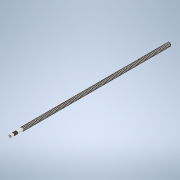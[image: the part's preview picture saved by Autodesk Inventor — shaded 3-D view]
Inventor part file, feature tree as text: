
AUTODESK INVENTOR PART (.ipt)
format: ipt  version: 2020.1 (Build 241239000, 239)  size: 3,920,384 bytes
history: native  units: mm
features: other x2, extrude x1, sketch x1
ambient origin geometry x8: Origin, YZ Plane, XZ Plane, XY Plane, X Axis, Y Axis, Z Axis, Center Point
bodies: Body1 (feature_tree)
feature tree (4):
  other  "Твердое тело1"
  extrude  "Выдавливание1"  Depth=100.0mm TaperAngle=0.0deg
  sketch  "Эскиз1"
  other  "Aesthetic Chamfer"
